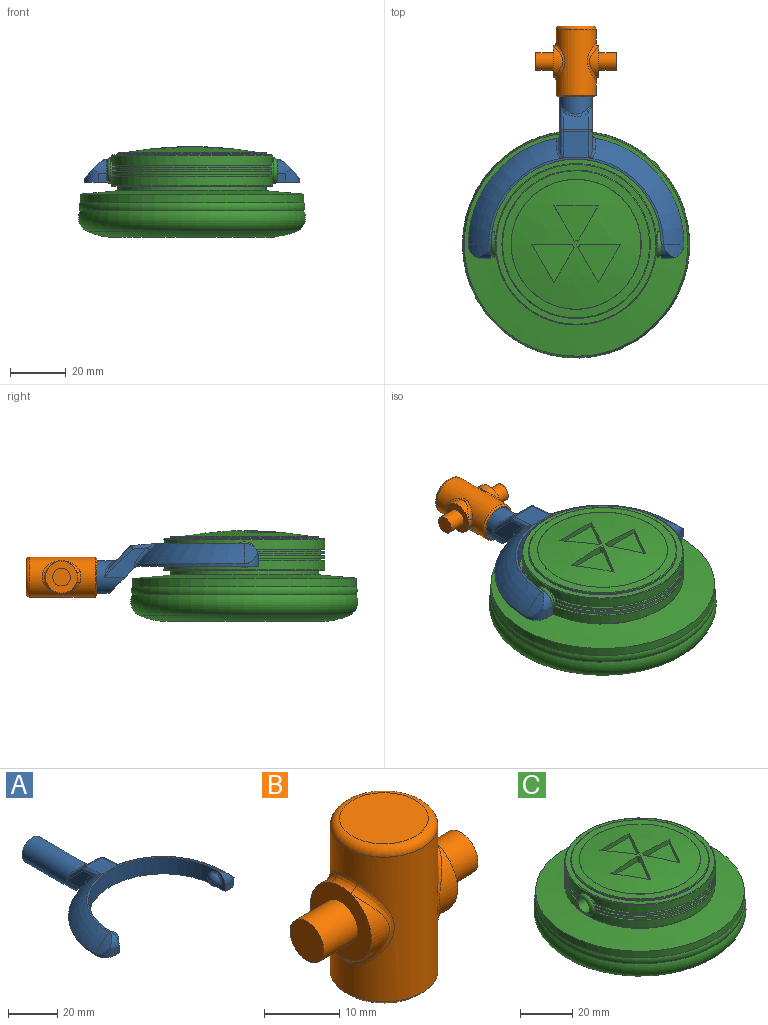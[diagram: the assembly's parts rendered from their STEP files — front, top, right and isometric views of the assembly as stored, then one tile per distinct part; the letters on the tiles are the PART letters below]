
ASSEMBLY  parts=3 mates=2
PART A: 48 faces, bbox 77.3x80.8x18.2 mm
  f0: plane 11.99x9.83mm, normal (0,-0.71,-0.71), area 141.5mm2, adj f1,f2,f9,f30,f43,f46
  f1: plane 15.39x10.49mm, normal (-1,0,0), area 63.5mm2, adj f0,f30,f32,f36,f46,f47
  f2: plane 15.39x10.49mm, normal (1,0,0), area 63.5mm2, adj f0,f30,f34,f39,f43,f44
  f3: plane 9.14x6.37mm, normal (0,0.71,0.71), area 67.6mm2, adj f35,f36,f39,f40
  f4: cylinder r=38.61mm len=37.99mm, axis (0,0,-1), area 42.6mm2, adj f6,f9,f17,f46,f47
  f5: torus R=19.3mm, axis (0,0,-1), area 507.8mm2, adj f10,f11,f12,f29,f42,f44
  f6: torus R=19.3mm, axis (0,0,-1), area 507.8mm2, adj f4,f11,f15,f28,f45,f47
  f7: cylinder r=30.48mm len=60.96mm, axis (0,0,-1), area 746.6mm2, adj f8,f9,f11,f14,f21,f24
  f8: plane 8.13x5.08mm, normal (-1,0,0), area 19.9mm2, adj f7,f9,f13,f19,f24
  f9: plane 77.22x43.73mm, normal (0,0,-1), area 956.2mm2, adj f0,f4,f7,f8,f10,f13,f14,f16
  f10: cylinder r=38.61mm len=37.99mm, axis (0,0,-1), area 42.6mm2, adj f5,f9,f20,f43,f44
  f11: plane 62.55x30.95mm, normal (0,0,1), area 75mm2, adj f5,f6,f7,f18,f19,f27
  f12: cylinder r=22.71mm len=7.33mm, axis (0,1,0), area 24.8mm2, adj f5,f19,f20
  f13: plane 3.05x3.05mm, normal (0,-1,0), area 9.3mm2, adj f8,f9,f19,f20
  f14: plane 8.13x5.08mm, normal (1,0,0), area 19.9mm2, adj f7,f9,f16,f18,f21
  f15: cylinder r=22.71mm len=7.33mm, axis (0,1,0), area 24.8mm2, adj f6,f17,f18
  f16: plane 3.05x3.05mm, normal (0,-1,0), area 9.3mm2, adj f9,f14,f17,f18
  f17: cylinder r=5.08mm len=5.08mm, axis (0,0,-1), area 21.9mm2, adj f4,f9,f15,f16,f18
  f18: cylinder r=5.08mm len=5.08mm, axis (-1,0,0), area 21.9mm2, adj f11,f14,f15,f16,f17
  f19: cylinder r=5.08mm len=5.08mm, axis (-1,0,0), area 21.9mm2, adj f8,f11,f12,f13,f20
  f20: cylinder r=5.08mm len=5.08mm, axis (0,0,-1), area 21.9mm2, adj f9,f10,f12,f13,f19
  f21: cylinder r=3.17mm len=6.35mm, axis (-1,0,0), area 12.7mm2, adj f7,f14,f23
  f22: plane 1.27x1.27mm, normal (1,0,0), area 1.3mm2, adj f23
  f23: torus R=0.64mm, axis (1,0,0), area 56.5mm2, adj f21,f22
  f24: cylinder r=3.17mm len=6.35mm, axis (1,0,0), area 12.7mm2, adj f7,f8,f26
  f25: plane 1.27x1.27mm, normal (-1,0,0), area 1.3mm2, adj f26
  f26: torus R=0.64mm, axis (-1,0,0), area 56.5mm2, adj f24,f25
  f27: plane 9.86x9.36mm, normal (0,0.09,1), area 85.6mm2, adj f11,f28,f29,f32,f34,f35,f42,f45
  f28: plane 1.04x0.17mm, normal (0,-1,0), area 0mm2, adj f6,f27,f45
  f29: plane 1.04x0.17mm, normal (0,-1,0), area 0mm2, adj f5,f27,f42
  f30: cylinder r=5.84mm len=33.01mm, axis (0,-1,0), area 1029.7mm2, adj f0,f1,f2,f31,f38,f40,f41
  f31: plane 11.68x11.68mm, normal (0,1,0), area 107.2mm2, adj f30
  f32: cylinder r=1.27mm len=9.13mm, axis (0,-1,0.09), area 14.4mm2, adj f1,f27,f33,f45
  f33: sphere r=1.27mm, area 1.5mm2, adj f32,f35,f36
  f34: cylinder r=1.27mm len=9.13mm, axis (0,1,-0.09), area 14.4mm2, adj f2,f27,f37,f42
  f35: cylinder r=1.27mm len=9.14mm, axis (-1,0,0), area 8.1mm2, adj f3,f27,f33,f37
  f36: cylinder r=1.27mm len=10.91mm, axis (0,-0.71,0.71), area 23.1mm2, adj f1,f3,f33,f38
  f37: sphere r=1.27mm, area 1.5mm2, adj f34,f35,f39
  f38: bspline ~4.55x2.75mm, area 2.3mm2, adj f30,f36,f40
  f39: cylinder r=1.27mm len=10.91mm, axis (0,0.71,-0.71), area 23.1mm2, adj f2,f3,f37,f41
  f40: bspline ~9.14x2.56mm, area 10.7mm2, adj f3,f30,f38,f41
  f41: bspline ~5.23x3.53mm, area 2.3mm2, adj f30,f39,f40
  f42: bspline ~4.62x3.14mm, area 5.2mm2, adj f5,f27,f29,f34,f44
  f43: cylinder r=1.27mm len=1.74mm, axis (0,0,-1), area 1.9mm2, adj f0,f2,f9,f10,f44
  f44: bspline ~8.6x7.86mm, area 11.9mm2, adj f2,f5,f10,f42,f43
  f45: bspline ~4.62x3.14mm, area 5.2mm2, adj f6,f27,f28,f32,f47
  f46: cylinder r=1.27mm len=1.74mm, axis (0,0,-1), area 1.9mm2, adj f0,f1,f4,f9,f47
  f47: bspline ~8.6x7.86mm, area 11.9mm2, adj f1,f4,f6,f45,f46
PART B: 25 faces, bbox 28.9x15.5x25.4 mm
  f0: cylinder r=5.71mm len=10.81mm, axis (-1,0,0), area 26.2mm2, adj f5,f15
  f1: cylinder r=5.71mm len=10.81mm, axis (-1,0,0), area 26.2mm2, adj f8,f11
  f2: cylinder r=7.14mm len=23.5mm, axis (0,0,-1), area 763.2mm2, adj f9,f10,f11,f12,f13,f14,f15,f16
  f3: plane 11.75x11.75mm, normal (0,0,1), area 108.4mm2, adj f17
  f4: plane 13.02x13.02mm, normal (0,0,-1), area 16.3mm2, adj f22,f24
  f5: plane 11.46x11.46mm, normal (1,0,0), area 70.9mm2, adj f0,f6,f13,f16,f18
  f6: cylinder r=5.71mm len=10.81mm, axis (-1,0,0), area 26.2mm2, adj f5,f14
  f7: cylinder r=5.71mm len=10.81mm, axis (-1,0,0), area 26.2mm2, adj f8,f10
  f8: plane 11.46x11.46mm, normal (-1,0,0), area 70.9mm2, adj f1,f7,f9,f12,f20
  f9: bspline ~4.64x1.73mm, area 6.5mm2, adj f2,f8,f10,f11
  f10: bspline ~13.62x4.91mm, area 20.7mm2, adj f2,f7,f9,f12
  f11: bspline ~13.6x4.87mm, area 20.7mm2, adj f1,f2,f9,f12
  f12: bspline ~4.64x1.73mm, area 6.5mm2, adj f2,f8,f10,f11
  f13: bspline ~4.64x1.73mm, area 6.5mm2, adj f2,f5,f14,f15
  f14: bspline ~13.62x4.91mm, area 20.7mm2, adj f2,f6,f13,f16
  f15: bspline ~13.6x4.87mm, area 20.7mm2, adj f0,f2,f13,f16
  f16: bspline ~4.64x1.73mm, area 6.5mm2, adj f2,f5,f14,f15
  f17: torus R=5.87mm, axis (0,0,1), area 83.8mm2, adj f2,f3
  f18: cylinder r=3.17mm len=6.35mm, axis (-1,0,0), area 126.7mm2, adj f5,f19
  f19: plane 6.35x6.35mm, normal (1,0,0), area 31.7mm2, adj f18
  f20: cylinder r=3.17mm len=6.35mm, axis (1,0,0), area 126.7mm2, adj f8,f21
  f21: plane 6.35x6.35mm, normal (-1,0,0), area 31.7mm2, adj f20
  f22: cylinder r=6.1mm len=22.86mm, axis (0,0,-1), area 875.6mm2, adj f4,f23
  f23: plane 12.19x12.19mm, normal (0,0,-1), area 116.7mm2, adj f22
  f24: cone r=7.14mm half-angle=45deg, axis (0,0,1), area 38.5mm2, adj f2,f4
PART C: 63 faces, bbox 96.2x96.2x32.5 mm
  f0: cylinder r=28.87mm len=57.73mm, axis (0,0,-1), area 595.7mm2, adj f1,f2,f53,f54,f59
  f1: plane 57.13x24.71mm, normal (0,0,1), area 102mm2, adj f0,f4,f53,f54
  f2: plane 57.13x24.71mm, normal (0,0,1), area 102mm2, adj f0,f3,f53,f54
  f3: cylinder r=27.6mm len=54.56mm, axis (0,0,1), area 49.6mm2, adj f2,f6,f53,f54
  f4: cylinder r=27.6mm len=54.56mm, axis (0,0,1), area 49.6mm2, adj f1,f5,f53,f54
  f5: plane 57.06x24.48mm, normal (0,0,-1), area 101.4mm2, adj f4,f7,f53,f54
  f6: plane 57.06x24.48mm, normal (0,0,-1), area 101.4mm2, adj f3,f8,f53,f54
  f7: cylinder r=28.87mm len=57.06mm, axis (0,0,-1), area 77.8mm2, adj f5,f13,f53,f54
  f8: cylinder r=28.87mm len=57.06mm, axis (0,0,-1), area 77.8mm2, adj f6,f14,f53,f54
  f9: cylinder r=27.6mm len=54.44mm, axis (0,0,1), area 49.2mm2, adj f12,f14,f53,f54
  f10: cylinder r=27.6mm len=54.44mm, axis (0,0,1), area 49.2mm2, adj f11,f13,f53,f54
  f11: plane 57.01x24.31mm, normal (0,0,-1), area 101mm2, adj f10,f15,f53,f54
  f12: plane 57.01x24.31mm, normal (0,0,-1), area 101mm2, adj f9,f16,f53,f54
  f13: plane 57.01x24.31mm, normal (0,0,1), area 101mm2, adj f7,f10,f53,f54
  f14: plane 57.01x24.31mm, normal (0,0,1), area 101mm2, adj f8,f9,f53,f54
  f15: cylinder r=28.87mm len=57.06mm, axis (0,0,-1), area 77.8mm2, adj f11,f19,f53,f54
  f16: cylinder r=28.87mm len=57.06mm, axis (0,0,-1), area 77.8mm2, adj f12,f20,f53,f54
  f17: plane 57.13x24.71mm, normal (0,0,-1), area 102mm2, adj f22,f23,f53,f54
  f18: plane 57.13x24.71mm, normal (0,0,-1), area 102mm2, adj f21,f23,f53,f54
  f19: plane 57.06x24.48mm, normal (0,0,1), area 101.4mm2, adj f15,f22,f53,f54
  f20: plane 57.06x24.48mm, normal (0,0,1), area 101.4mm2, adj f16,f21,f53,f54
  f21: cylinder r=27.6mm len=54.56mm, axis (0,0,1), area 49.6mm2, adj f18,f20,f53,f54
  f22: cylinder r=27.6mm len=54.56mm, axis (0,0,1), area 49.6mm2, adj f17,f19,f53,f54
  f23: cylinder r=28.87mm len=57.73mm, axis (0,0,-1), area 595.8mm2, adj f17,f18,f53,f54,f60
  f24: sphere r=135.39mm, area 1385.3mm2, adj f37,f38,f39,f40,f42,f43,f44,f45
  f25: plane 39.33x39.33mm, normal (0,0,-1), area 1214.6mm2, adj f26
  f26: torus R=20.12mm, axis (0,0,-1), area 1429.3mm2, adj f25,f27
  f27: torus R=27.74mm, axis (0,0,-1), area 3542.1mm2, adj f26,f28
  f28: torus R=35.36mm, axis (0,0,-1), area 2180.1mm2, adj f27,f29
  f29: torus R=37.35mm, axis (0,0,-1), area 734.6mm2, adj f28,f30
  f30: cylinder r=40.06mm len=80.11mm, axis (0,0,-1), area 799.1mm2, adj f29,f31
  f31: cone r=26.57mm half-angle=85deg, axis (0,0,-1), area 2833.8mm2, adj f30,f32
  f32: cylinder r=26.57mm len=53.14mm, axis (0,0,-1), area 265mm2, adj f31,f33
  f33: plane 57.23x57.23mm, normal (0,0,-1), area 354.5mm2, adj f32,f59
  f34: cone r=26.57mm half-angle=87deg, axis (0,0,-1), area 475.4mm2, adj f61,f62
  f35: cylinder r=26.57mm len=53.14mm, axis (0,0,-1), area 92.3mm2, adj f36,f61
  f36: plane 57.23x57.23mm, normal (0,0,1), area 354.5mm2, adj f35,f60
  f37: plane 14.61x2.53mm, normal (0,-1,0), area 32.2mm2, adj f24,f38,f40,f41
  f38: cylinder r=1.27mm len=2.53mm, axis (0,0,1), area 3.4mm2, adj f24,f37,f39,f41
  f39: plane 12.65x7.3mm, normal (0.87,0.5,0), area 32.2mm2, adj f24,f38,f40,f41
  f40: plane 13.75x7.94mm, normal (-0.87,0.5,0), area 28mm2, adj f24,f37,f39,f41
  f41: plane 15.24x13.75mm, normal (0,0,1), area 108.3mm2, adj f37,f38,f39,f40
  f42: cylinder r=1.27mm len=2.53mm, axis (0,0,1), area 3.4mm2, adj f24,f43,f45,f46
  f43: plane 14.61x2.53mm, normal (0,-1,0), area 32.2mm2, adj f24,f42,f44,f46
  f44: plane 13.75x7.94mm, normal (0.87,0.5,0), area 28mm2, adj f24,f43,f45,f46
  f45: plane 12.65x7.3mm, normal (-0.87,0.5,0), area 32.2mm2, adj f24,f42,f44,f46
  f46: plane 15.24x13.75mm, normal (0,0,1), area 108.3mm2, adj f42,f43,f44,f45
  f47: cylinder r=1.27mm len=2.53mm, axis (0,0,1), area 3.4mm2, adj f24,f48,f50,f51
  f48: plane 12.65x7.3mm, normal (-0.87,0.5,0), area 32.2mm2, adj f24,f47,f49,f51
  f49: plane 15.88x1.84mm, normal (0,-1,0), area 28mm2, adj f24,f48,f50,f51
  f50: plane 12.65x7.3mm, normal (0.87,0.5,0), area 32.2mm2, adj f24,f47,f49,f51
  f51: plane 15.88x12.65mm, normal (0,0,1), area 108.3mm2, adj f47,f48,f49,f50
  f52: plane 6.6x6.6mm, normal (1,0,0), area 2.6mm2, adj f57,f58
  f53: cylinder r=4.57mm len=9.14mm, axis (-1,0,0), area 20.2mm2, adj f0,f1,f2,f3,f4,f5,f6,f7
  f54: cylinder r=4.57mm len=9.14mm, axis (-1,0,0), area 20.2mm2, adj f0,f1,f2,f3,f4,f5,f6,f7
  f55: plane 6.6x6.6mm, normal (-1,0,0), area 2.6mm2, adj f56,f58
  f56: torus R=3.3mm, axis (1,0,0), area 51.5mm2, adj f54,f55
  f57: torus R=3.3mm, axis (1,0,0), area 51.5mm2, adj f52,f53
  f58: cylinder r=3.17mm len=60.96mm, axis (1,0,0), area 1216.1mm2, adj f52,f55
  f59: torus R=28.61mm, axis (0,0,1), area 72.1mm2, adj f0,f33
  f60: torus R=28.61mm, axis (0,0,-1), area 72.1mm2, adj f23,f36
  f61: torus R=26.31mm, axis (0,0,1), area 64.2mm2, adj f34,f35
  f62: torus R=23.29mm, axis (0,0,1), area 4.5mm2, adj f24,f34
PLACE A t=(32.34,27.52,20.85)mm
PLACE B rot(axis=(-1,0,0),90deg) t=(32.34,80.3,16.88)mm
PLACE C t=(32.34,27.52,33.52)mm
MATE revolute A.f24 <-> C.f53  axis (-1,0,0) through (62.82,27.52,24.92)mm
MATE revolute B.f2 <-> A.f30  axis (0,-1,0) through (32.34,103.16,16.88)mm
